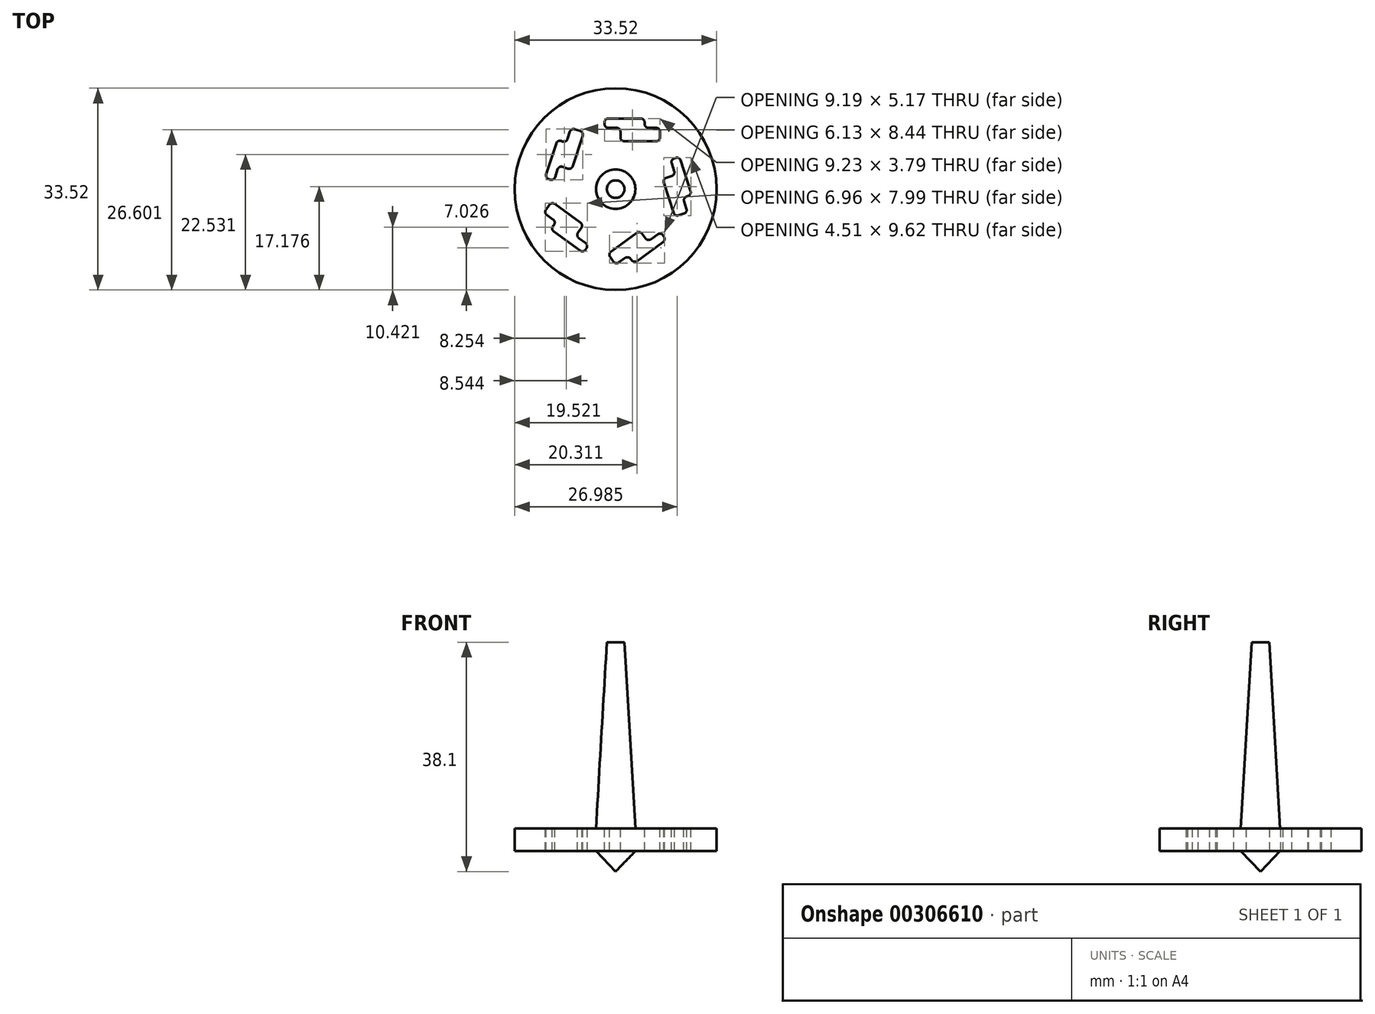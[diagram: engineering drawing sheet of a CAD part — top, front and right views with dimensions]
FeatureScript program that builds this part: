
annotation { "Feature Type Name" : "Feature", "Feature Type Description" : "" }
export const myFeature = defineFeature(function(context is Context, id is Id, definition is map)
    precondition{}
    {
        {
            var Q0;
            Q0=qCreatedBy(makeId("Front.planeOp"),FACE);
            var sketch = newSketch(context, id + "F0", { "sketchPlane" : qUnion([Q0])});
            skLineSegment(sketch, "E0", {"start": v(0, 0) * mm, "end": v(0, 38.1) * mm});
            skLineSegment(sketch, "E1", {"start": v(3.27, 7.16) * mm, "end": v(16.76, 7.16) * mm});
            skLineSegment(sketch, "E2", {"start": v(16.76, 7.16) * mm, "end": v(16.76, 3.38) * mm});
            skLineSegment(sketch, "E3", {"start": v(16.76, 3.38) * mm, "end": v(3.27, 3.38) * mm});
            skLineSegment(sketch, "E4", {"start": v(3.27, 3.38) * mm, "end": v(0, 0) * mm});
            skLineSegment(sketch, "E5", {"start": v(3.27, 7.16) * mm, "end": v(1.46, 38.1) * mm});
            skLineSegment(sketch, "E6", {"start": v(1.46, 38.1) * mm, "end": v(0, 38.1) * mm});
            skSolve(sketch);
        }
        {
            var Q0;
            Q0 = qSketchRegion(id + "F0", true);
            var Q1;
            Q1=sQuery(id+"F0.wireOp",EDGE,"E0");
            revolve(context, id + "F1", {"entities" : qUnion([Q0]), "axis" : qUnion([Q1]), "revolveType" : RevolveType.FULL});
        }
        {
            var Q0;
            Q0=makeQuery(id+"F1.opRevolve","SWEPT_FACE",FACE,{"disambiguationData":[OSD([sQuery(id+"F0.wireOp",EDGE,"E1")])]});
            var sketch = newSketch(context, id + "F2", { "sketchPlane" : qUnion([Q0])});
            skLineSegment(sketch, "E7.bottom", {"start": v(-1.22, 11.74) * mm, "end": v(4.17, 11.74) * mm});
            skLineSegment(sketch, "E7.top", {"start": v(-1.22, 10.18) * mm, "end": v(0.17, 10.18) * mm});
            skLineSegment(sketch, "E7.left", {"start": v(-1.85, 11.1) * mm, "end": v(-1.85, 10.81) * mm});
            skLineSegment(sketch, "E7.right", {"start": v(4.8, 11.1) * mm, "end": v(4.8, 10.81) * mm});
            skLineSegment(sketch, "E8.bottom", {"start": v(5.44, 10.18) * mm, "end": v(6.74, 10.18) * mm});
            skLineSegment(sketch, "E8.top", {"start": v(1.44, 7.94) * mm, "end": v(6.74, 7.94) * mm});
            skLineSegment(sketch, "E8.left", {"start": v(0.8, 9.54) * mm, "end": v(0.8, 8.58) * mm});
            skLineSegment(sketch, "E8.right", {"start": v(7.38, 9.54) * mm, "end": v(7.38, 8.58) * mm});
            skPoint(sketch, "E9.visualSharp", {"position": v(-1.85, 11.74) * mm});
            skArc(sketch, "E9.filletArc", {"start": v(-1.22, 11.74) * mm, "mid": v(-1.67, 11.55) * mm, "end": v(-1.85, 11.1) * mm});
            skPoint(sketch, "E10.visualSharp", {"position": v(-1.85, 10.18) * mm});
            skArc(sketch, "E10.filletArc", {"start": v(-1.85, 10.81) * mm, "mid": v(-1.67, 10.36) * mm, "end": v(-1.22, 10.18) * mm});
            skPoint(sketch, "E11.visualSharp", {"position": v(0.8, 10.18) * mm});
            skArc(sketch, "E11.filletArc", {"start": v(0.8, 9.54) * mm, "mid": v(0.61, 10) * mm, "end": v(0.17, 10.18) * mm});
            skPoint(sketch, "E12.visualSharp", {"position": v(0.8, 7.94) * mm});
            skArc(sketch, "E12.filletArc", {"start": v(0.8, 8.58) * mm, "mid": v(0.99, 8.13) * mm, "end": v(1.44, 7.94) * mm});
            skPoint(sketch, "E13.visualSharp", {"position": v(7.38, 7.94) * mm});
            skArc(sketch, "E13.filletArc", {"start": v(6.74, 7.94) * mm, "mid": v(7.19, 8.13) * mm, "end": v(7.38, 8.58) * mm});
            skPoint(sketch, "E14.visualSharp", {"position": v(7.38, 10.18) * mm});
            skArc(sketch, "E14.filletArc", {"start": v(7.38, 9.54) * mm, "mid": v(7.19, 10) * mm, "end": v(6.74, 10.18) * mm});
            skPoint(sketch, "E15.visualSharp", {"position": v(4.8, 10.18) * mm});
            skArc(sketch, "E15.filletArc", {"start": v(4.8, 10.81) * mm, "mid": v(5, 10.36) * mm, "end": v(5.44, 10.18) * mm});
            skPoint(sketch, "E16.visualSharp", {"position": v(4.8, 11.74) * mm});
            skArc(sketch, "E16.filletArc", {"start": v(4.8, 11.1) * mm, "mid": v(4.62, 11.55) * mm, "end": v(4.17, 11.74) * mm});
            skPoint(sketch, "E17.1.0", {"position": v(-5.28, 9.47) * mm});
            skPoint(sketch, "E17.1.1", {"position": v(-7.4, 10.16) * mm});
            skPoint(sketch, "E17.1.2", {"position": v(-9.68, 8.2) * mm});
            skPoint(sketch, "E17.1.3", {"position": v(-7.3, 3.22) * mm});
            skPoint(sketch, "E17.1.4", {"position": v(-8.2, 7.71) * mm});
            skPoint(sketch, "E17.1.5", {"position": v(-9.43, 3.9) * mm});
            skPoint(sketch, "E17.1.6", {"position": v(-11.74, 1.86) * mm});
            skPoint(sketch, "E17.1.7", {"position": v(-10.25, 1.38) * mm});
            skLineSegment(sketch, "E17.1.8", {"start": v(-11.54, 2.47) * mm, "end": v(-9.87, 7.6) * mm});
            skLineSegment(sketch, "E17.1.9", {"start": v(-10.06, 1.99) * mm, "end": v(-9.63, 3.3) * mm});
            skLineSegment(sketch, "E17.1.10", {"start": v(-8, 8.32) * mm, "end": v(-7.6, 9.56) * mm});
            skLineSegment(sketch, "E17.1.11", {"start": v(-7.11, 3.82) * mm, "end": v(-5.47, 8.87) * mm});
            skArc(sketch, "E17.1.12", {"start": v(-6.8, 9.96) * mm, "mid": v(-7.28, 9.93) * mm, "end": v(-7.6, 9.56) * mm});
            skArc(sketch, "E17.1.13", {"start": v(-7.91, 3.41) * mm, "mid": v(-7.43, 3.45) * mm, "end": v(-7.11, 3.82) * mm});
            skArc(sketch, "E17.1.14", {"start": v(-8.83, 3.71) * mm, "mid": v(-9.31, 3.67) * mm, "end": v(-9.63, 3.3) * mm});
            skArc(sketch, "E17.1.15", {"start": v(-8.8, 7.91) * mm, "mid": v(-8.31, 7.95) * mm, "end": v(-8, 8.32) * mm});
            skArc(sketch, "E17.1.16", {"start": v(-9.07, 8) * mm, "mid": v(-9.56, 7.96) * mm, "end": v(-9.87, 7.6) * mm});
            skArc(sketch, "E17.1.17", {"start": v(-5.47, 8.87) * mm, "mid": v(-5.51, 9.35) * mm, "end": v(-5.88, 9.67) * mm});
            skArc(sketch, "E17.1.18", {"start": v(-10.86, 1.58) * mm, "mid": v(-10.37, 1.62) * mm, "end": v(-10.06, 1.99) * mm});
            skArc(sketch, "E17.1.19", {"start": v(-11.54, 2.47) * mm, "mid": v(-11.5, 1.98) * mm, "end": v(-11.13, 1.67) * mm});
            skLineSegment(sketch, "E17.1.20", {"start": v(-6.8, 9.96) * mm, "end": v(-5.88, 9.67) * mm});
            skLineSegment(sketch, "E17.1.21", {"start": v(-8.83, 3.71) * mm, "end": v(-7.91, 3.41) * mm});
            skLineSegment(sketch, "E17.1.22", {"start": v(-11.13, 1.67) * mm, "end": v(-10.86, 1.58) * mm});
            skLineSegment(sketch, "E17.1.23", {"start": v(-9.07, 8) * mm, "end": v(-8.8, 7.91) * mm});
            skPoint(sketch, "E17.2.0", {"position": v(-10.64, -2.1) * mm});
            skPoint(sketch, "E17.2.1", {"position": v(-11.95, -3.9) * mm});
            skPoint(sketch, "E17.2.2", {"position": v(-10.79, -6.67) * mm});
            skPoint(sketch, "E17.2.3", {"position": v(-5.32, -5.96) * mm});
            skPoint(sketch, "E17.2.4", {"position": v(-9.87, -5.41) * mm});
            skPoint(sketch, "E17.2.5", {"position": v(-6.63, -7.76) * mm});
            skPoint(sketch, "E17.2.6", {"position": v(-5.4, -10.59) * mm});
            skPoint(sketch, "E17.2.7", {"position": v(-4.48, -9.32) * mm});
            skLineSegment(sketch, "E17.2.8", {"start": v(-5.91, -10.21) * mm, "end": v(-10.27, -7.04) * mm});
            skLineSegment(sketch, "E17.2.9", {"start": v(-5, -8.95) * mm, "end": v(-6.12, -8.14) * mm});
            skLineSegment(sketch, "E17.2.10", {"start": v(-10.38, -5.04) * mm, "end": v(-11.44, -4.27) * mm});
            skLineSegment(sketch, "E17.2.11", {"start": v(-5.83, -5.58) * mm, "end": v(-10.12, -2.47) * mm});
            skArc(sketch, "E17.2.12", {"start": v(-11.58, -3.39) * mm, "mid": v(-11.69, -3.86) * mm, "end": v(-11.44, -4.27) * mm});
            skArc(sketch, "E17.2.13", {"start": v(-5.7, -6.47) * mm, "mid": v(-5.58, -6) * mm, "end": v(-5.83, -5.58) * mm});
            skArc(sketch, "E17.2.14", {"start": v(-6.26, -7.25) * mm, "mid": v(-6.37, -7.72) * mm, "end": v(-6.12, -8.14) * mm});
            skArc(sketch, "E17.2.15", {"start": v(-10.24, -5.92) * mm, "mid": v(-10.13, -5.45) * mm, "end": v(-10.38, -5.04) * mm});
            skArc(sketch, "E17.2.16", {"start": v(-10.41, -6.16) * mm, "mid": v(-10.53, -6.63) * mm, "end": v(-10.27, -7.04) * mm});
            skArc(sketch, "E17.2.17", {"start": v(-10.12, -2.47) * mm, "mid": v(-10.6, -2.35) * mm, "end": v(-11, -2.6) * mm});
            skArc(sketch, "E17.2.18", {"start": v(-4.86, -9.84) * mm, "mid": v(-4.74, -9.37) * mm, "end": v(-5, -8.95) * mm});
            skArc(sketch, "E17.2.19", {"start": v(-5.91, -10.21) * mm, "mid": v(-5.44, -10.33) * mm, "end": v(-5.03, -10.07) * mm});
            skLineSegment(sketch, "E17.2.20", {"start": v(-11.58, -3.39) * mm, "end": v(-11, -2.6) * mm});
            skLineSegment(sketch, "E17.2.21", {"start": v(-6.26, -7.25) * mm, "end": v(-5.7, -6.47) * mm});
            skLineSegment(sketch, "E17.2.22", {"start": v(-5.03, -10.07) * mm, "end": v(-4.86, -9.84) * mm});
            skLineSegment(sketch, "E17.2.23", {"start": v(-10.41, -6.16) * mm, "end": v(-10.24, -5.92) * mm});
            skPoint(sketch, "E17.3.0", {"position": v(-1.3, -10.76) * mm});
            skPoint(sketch, "E17.3.1", {"position": v(0.02, -12.57) * mm});
            skPoint(sketch, "E17.3.2", {"position": v(3.01, -12.32) * mm});
            skPoint(sketch, "E17.3.3", {"position": v(4.02, -6.9) * mm});
            skPoint(sketch, "E17.3.4", {"position": v(2.1, -11.06) * mm});
            skPoint(sketch, "E17.3.5", {"position": v(5.33, -8.7) * mm});
            skPoint(sketch, "E17.3.6", {"position": v(8.4, -8.4) * mm});
            skPoint(sketch, "E17.3.7", {"position": v(7.48, -7.14) * mm});
            skLineSegment(sketch, "E17.3.8", {"start": v(7.89, -8.78) * mm, "end": v(3.53, -11.95) * mm});
            skLineSegment(sketch, "E17.3.9", {"start": v(6.97, -7.52) * mm, "end": v(5.85, -8.33) * mm});
            skLineSegment(sketch, "E17.3.10", {"start": v(1.58, -11.43) * mm, "end": v(0.53, -12.2) * mm});
            skLineSegment(sketch, "E17.3.11", {"start": v(3.5, -7.27) * mm, "end": v(-0.78, -10.39) * mm});
            skArc(sketch, "E17.3.12", {"start": v(-0.36, -12.06) * mm, "mid": v(0.06, -12.3) * mm, "end": v(0.53, -12.2) * mm});
            skArc(sketch, "E17.3.13", {"start": v(4.4, -7.41) * mm, "mid": v(3.98, -7.16) * mm, "end": v(3.5, -7.27) * mm});
            skArc(sketch, "E17.3.14", {"start": v(4.96, -8.2) * mm, "mid": v(5.38, -8.45) * mm, "end": v(5.85, -8.33) * mm});
            skArc(sketch, "E17.3.15", {"start": v(2.47, -11.57) * mm, "mid": v(2.05, -11.32) * mm, "end": v(1.58, -11.43) * mm});
            skArc(sketch, "E17.3.16", {"start": v(2.64, -11.8) * mm, "mid": v(3.05, -12.06) * mm, "end": v(3.53, -11.95) * mm});
            skArc(sketch, "E17.3.17", {"start": v(-0.78, -10.39) * mm, "mid": v(-1.04, -10.8) * mm, "end": v(-0.92, -11.28) * mm});
            skArc(sketch, "E17.3.18", {"start": v(7.86, -7.66) * mm, "mid": v(7.44, -7.4) * mm, "end": v(6.97, -7.52) * mm});
            skArc(sketch, "E17.3.19", {"start": v(7.89, -8.78) * mm, "mid": v(8.14, -8.36) * mm, "end": v(8.03, -7.9) * mm});
            skLineSegment(sketch, "E17.3.20", {"start": v(-0.36, -12.06) * mm, "end": v(-0.92, -11.28) * mm});
            skLineSegment(sketch, "E17.3.21", {"start": v(4.96, -8.2) * mm, "end": v(4.4, -7.41) * mm});
            skLineSegment(sketch, "E17.3.22", {"start": v(8.03, -7.9) * mm, "end": v(7.86, -7.66) * mm});
            skLineSegment(sketch, "E17.3.23", {"start": v(2.64, -11.8) * mm, "end": v(2.47, -11.57) * mm});
            skPoint(sketch, "E17.4.0", {"position": v(9.83, -4.56) * mm});
            skPoint(sketch, "E17.4.1", {"position": v(11.96, -3.87) * mm});
            skPoint(sketch, "E17.4.2", {"position": v(12.65, -0.94) * mm});
            skPoint(sketch, "E17.4.3", {"position": v(7.8, 1.7) * mm});
            skPoint(sketch, "E17.4.4", {"position": v(11.16, -1.42) * mm});
            skPoint(sketch, "E17.4.5", {"position": v(9.93, 2.38) * mm});
            skPoint(sketch, "E17.4.6", {"position": v(10.59, 5.4) * mm});
            skPoint(sketch, "E17.4.7", {"position": v(9.1, 4.9) * mm});
            skLineSegment(sketch, "E17.4.8", {"start": v(10.79, 4.79) * mm, "end": v(12.45, -0.34) * mm});
            skLineSegment(sketch, "E17.4.9", {"start": v(9.3, 4.3) * mm, "end": v(9.73, 2.99) * mm});
            skLineSegment(sketch, "E17.4.10", {"start": v(11.36, -2.03) * mm, "end": v(11.76, -3.27) * mm});
            skLineSegment(sketch, "E17.4.11", {"start": v(8, 1.09) * mm, "end": v(9.64, -3.96) * mm});
            skArc(sketch, "E17.4.12", {"start": v(11.36, -4.07) * mm, "mid": v(11.72, -3.75) * mm, "end": v(11.76, -3.27) * mm});
            skArc(sketch, "E17.4.13", {"start": v(8.4, 1.89) * mm, "mid": v(8.04, 1.57) * mm, "end": v(8, 1.09) * mm});
            skArc(sketch, "E17.4.14", {"start": v(9.32, 2.19) * mm, "mid": v(9.7, 2.5) * mm, "end": v(9.73, 2.99) * mm});
            skArc(sketch, "E17.4.15", {"start": v(11.77, -1.23) * mm, "mid": v(11.4, -1.54) * mm, "end": v(11.36, -2.03) * mm});
            skArc(sketch, "E17.4.16", {"start": v(12.04, -1.14) * mm, "mid": v(12.41, -0.82) * mm, "end": v(12.45, -0.34) * mm});
            skArc(sketch, "E17.4.17", {"start": v(9.64, -3.96) * mm, "mid": v(9.95, -4.33) * mm, "end": v(10.44, -4.36) * mm});
            skArc(sketch, "E17.4.18", {"start": v(9.71, 5.1) * mm, "mid": v(9.34, 4.79) * mm, "end": v(9.3, 4.3) * mm});
            skArc(sketch, "E17.4.19", {"start": v(10.79, 4.79) * mm, "mid": v(10.47, 5.16) * mm, "end": v(9.99, 5.2) * mm});
            skLineSegment(sketch, "E17.4.20", {"start": v(11.36, -4.07) * mm, "end": v(10.44, -4.36) * mm});
            skLineSegment(sketch, "E17.4.21", {"start": v(9.32, 2.19) * mm, "end": v(8.4, 1.89) * mm});
            skLineSegment(sketch, "E17.4.22", {"start": v(9.99, 5.2) * mm, "end": v(9.71, 5.1) * mm});
            skLineSegment(sketch, "E17.4.23", {"start": v(12.04, -1.14) * mm, "end": v(11.77, -1.23) * mm});
            skPoint(sketch, "E17.center", {"position": v(0, 0) * mm});
            skSolve(sketch);
        }
        {
            var Q0;
            Q0 = qSketchRegion(id + "F2", true);
            extrude(context, id + "F3", {"entities" : qUnion([Q0]), "operationType" : NewBodyOperationType.REMOVE, "endBound" : BoundingType.THROUGH_ALL, "oppositeDirection" : true, "depth" : 25.4 * mm});
        }
    });
